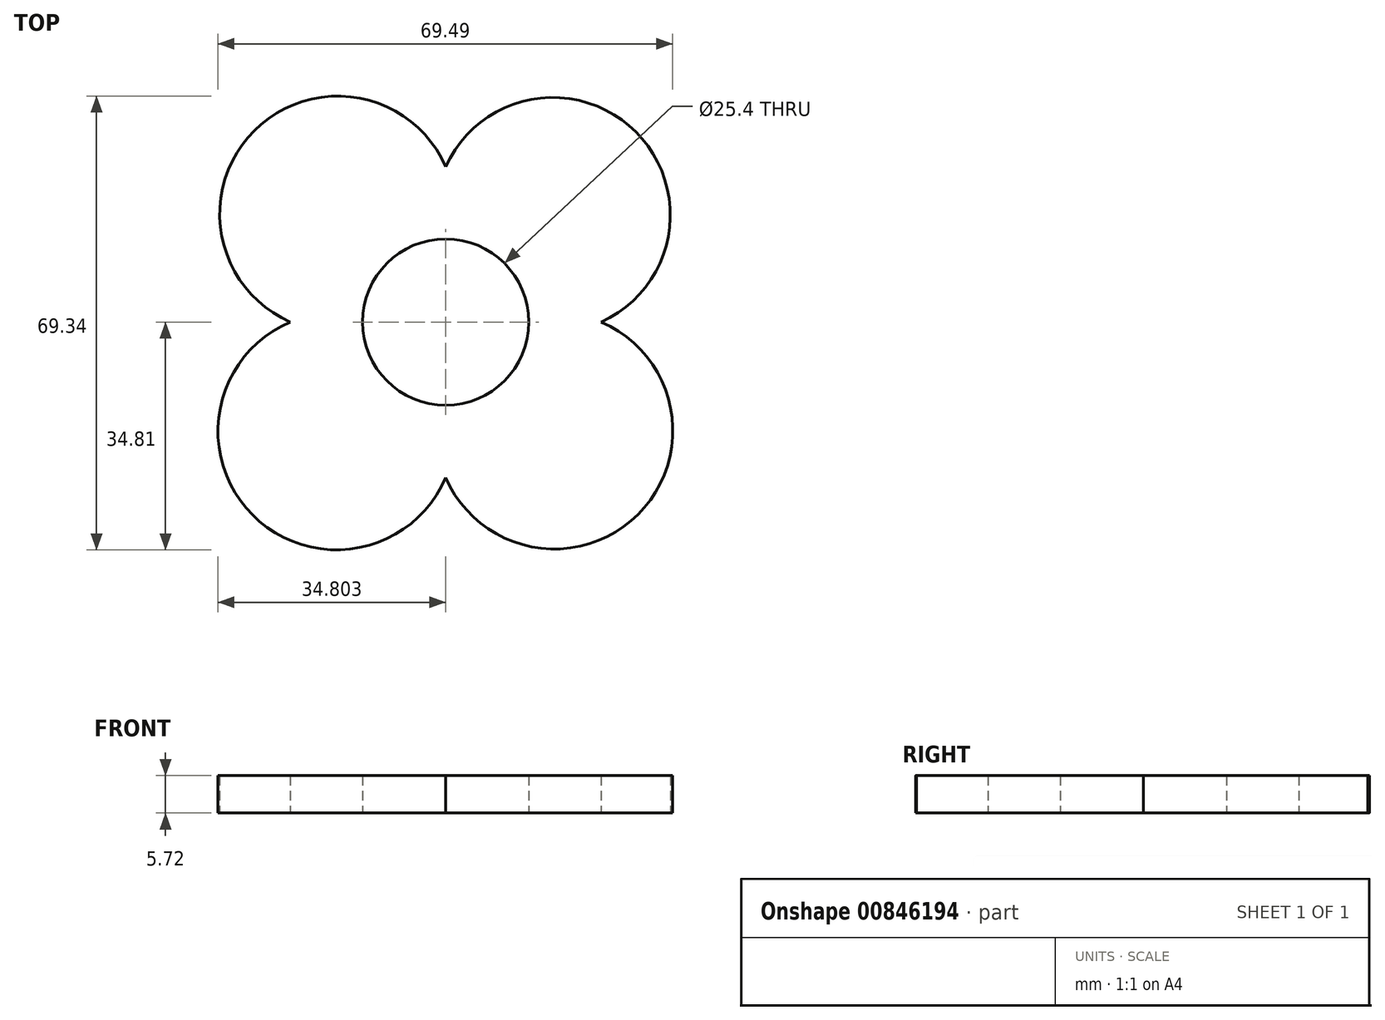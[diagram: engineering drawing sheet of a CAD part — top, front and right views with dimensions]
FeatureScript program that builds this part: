
annotation { "Feature Type Name" : "Feature", "Feature Type Description" : "" }
export const myFeature = defineFeature(function(context is Context, id is Id, definition is map)
    precondition{}
    {
        {
            var Q0;
            Q0=qCreatedBy(makeId("Top.planeOp"),FACE);
            var sketch = newSketch(context, id + "F0", { "sketchPlane" : qUnion([Q0])});
            skCircle(sketch, "E0", {"center": v(-12.47, -1.38) * mm, "radius": 11.05 * mm});
            skLineSegment(sketch, "E1", {"start": v(-12.47, 9.67) * mm, "end": v(-12.47, 22.37) * mm});
            skLineSegment(sketch, "E2", {"start": v(-1.42, -1.38) * mm, "end": v(11.28, -1.38) * mm});
            skLineSegment(sketch, "E3", {"start": v(-12.47, -12.43) * mm, "end": v(-12.47, -25.13) * mm});
            skLineSegment(sketch, "E4", {"start": v(-23.52, -1.38) * mm, "end": v(-36.22, -1.38) * mm});
            skCircle(sketch, "E5", {"center": v(-12.47, -1.38) * mm, "radius": 12.7 * mm});
            skArc(sketch, "E6", {"start": v(11.28, -1.38) * mm, "mid": v(16.59, 27.67) * mm, "end": v(-12.47, 22.37) * mm});
            skArc(sketch, "E7", {"start": v(-12.47, -25.13) * mm, "mid": v(16.92, -30.77) * mm, "end": v(11.28, -1.38) * mm});
            skArc(sketch, "E8", {"start": v(-36.22, -1.38) * mm, "mid": v(-41.96, -30.88) * mm, "end": v(-12.47, -25.13) * mm});
            skArc(sketch, "E9", {"start": v(-12.47, 22.37) * mm, "mid": v(-41.72, 27.87) * mm, "end": v(-36.22, -1.38) * mm});
            skSolve(sketch);
        }
        {
            var Q0;
            Q0 = qSketchRegion(id + "F0", true);
            extrude(context, id + "F1", {"entities" : qUnion([Q0]), "depth" : 5.7 * mm, "offsetDistance" : 25.4 * mm});
        }
    });
